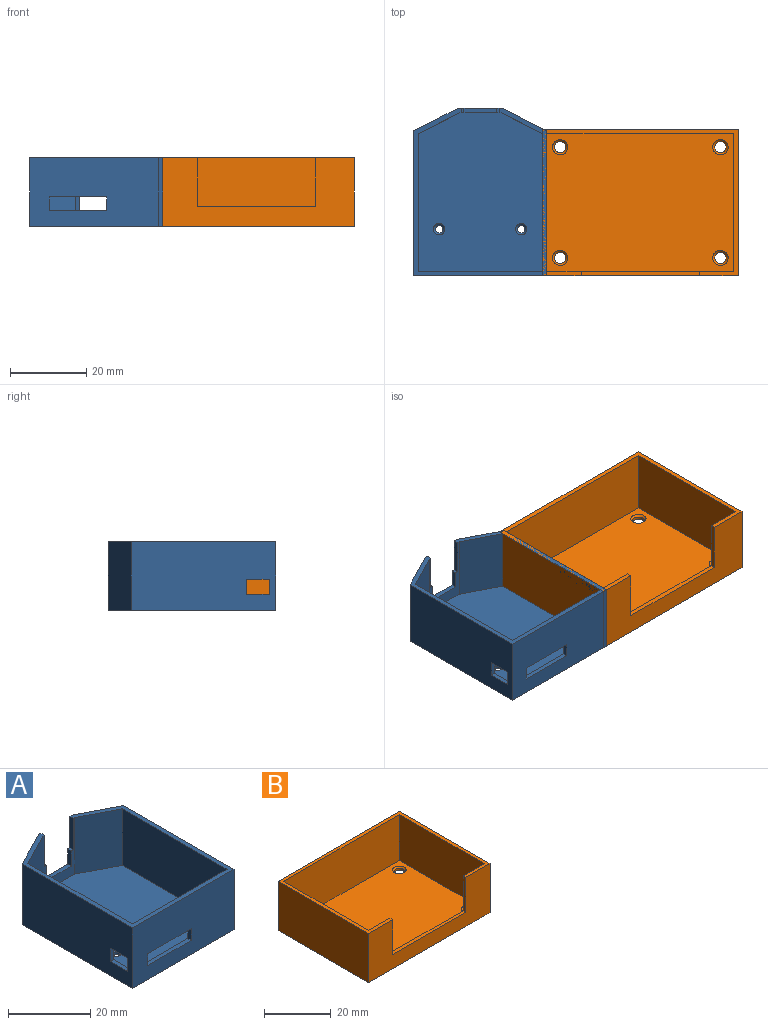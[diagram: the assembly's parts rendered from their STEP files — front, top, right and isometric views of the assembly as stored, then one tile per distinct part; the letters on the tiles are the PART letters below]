
ASSEMBLY  parts=2 mates=1
PART A: 34 faces, bbox 34.9x43.9x18 mm
  f0: plane 37.93x18mm, normal (-1,0,0), area 658.8mm2, adj f2,f4,f5,f9,f26,f27,f28,f29
  f1: plane 36x16.8mm, normal (1,0,0), area 580.8mm2, adj f3,f4,f10,f14,f26,f27,f28,f29
  f2: plane 34.9x18mm, normal (0,-1,0), area 575.7mm2, adj f0,f4,f6,f9,f22,f23,f24,f25
  f3: plane 32.5x16.8mm, normal (0,1,0), area 493.5mm2, adj f1,f4,f11,f14,f22,f23,f24,f25
  f4: plane 43.9x34.9mm, normal (0,0,1), area 160.9mm2, adj f0,f1,f2,f3,f5,f6,f7,f8
  f5: plane 18x11.66mm, normal (-0.46,0.89,0), area 235.8mm2, adj f0,f4,f8,f9
  f6: plane 37.93x18mm, normal (1,0,0), area 682.8mm2, adj f2,f4,f7,f9
  f7: plane 18x11.66mm, normal (0.46,0.89,0), area 235.8mm2, adj f4,f6,f8,f9
  f8: plane 18x11.58mm, normal (0,1,0), area 77.2mm2, adj f4,f5,f7,f9,f15,f16,f17,f18
  f9: plane 43.9x34.9mm, normal (0,0,-1), area 1456.3mm2, adj f0,f2,f5,f6,f7,f8,f30,f31
  f10: plane 16.8x10.75mm, normal (0.46,-0.89,0), area 202.9mm2, adj f1,f4,f13,f14
  f11: plane 36x16.8mm, normal (-1,0,0), area 604.8mm2, adj f3,f4,f12,f14
  f12: plane 16.8x10.75mm, normal (-0.46,-0.89,0), area 202.9mm2, adj f4,f11,f13,f14
  f13: plane 16.8x11mm, normal (0,-1,0), area 53.5mm2, adj f4,f10,f12,f14,f15,f16,f17,f18
  f14: plane 41.5x32.5mm, normal (0,0,1), area 1275.5mm2, adj f1,f3,f10,f11,f12,f13,f32,f33
  f15: plane 4.5x1.2mm, normal (1,0,0), area 5.4mm2, adj f8,f13,f16,f21
  f16: plane 1.2x0.75mm, normal (0,0,1), area 0.9mm2, adj f8,f13,f15,f17
  f17: plane 9.3x1.2mm, normal (1,0,0), area 11.2mm2, adj f4,f8,f13,f16
  f18: plane 9.3x1.2mm, normal (-1,0,0), area 11.2mm2, adj f4,f8,f13,f19
  f19: plane 1.2x0.75mm, normal (0,0,1), area 0.9mm2, adj f8,f13,f18,f20
  f20: plane 4.5x1.2mm, normal (-1,0,0), area 5.4mm2, adj f8,f13,f19,f21
  f21: plane 8.5x1.2mm, normal (0,0,1), area 10.2mm2, adj f8,f13,f15,f20
  f22: plane 15x1.2mm, normal (0,0,1), area 18mm2, adj f2,f3,f23,f25
  f23: plane 3.5x1.2mm, normal (-1,0,0), area 4.2mm2, adj f2,f3,f22,f24
  f24: plane 15x1.2mm, normal (0,0,-1), area 18mm2, adj f2,f3,f23,f25
  f25: plane 3.5x1.2mm, normal (1,0,0), area 4.2mm2, adj f2,f3,f22,f24
  f26: plane 4x1.2mm, normal (0,1,0), area 4.8mm2, adj f0,f1,f27,f29
  f27: plane 6x1.2mm, normal (0,0,-1), area 7.2mm2, adj f0,f1,f26,f28
  f28: plane 4x1.2mm, normal (0,-1,0), area 4.8mm2, adj f0,f1,f27,f29
  f29: plane 6x1.2mm, normal (0,0,1), area 7.2mm2, adj f0,f1,f26,f28
  f30: cylinder r=1mm len=2mm, axis (0,0,-1), area 4.4mm2, adj f9,f32
  f31: cylinder r=1mm len=2mm, axis (0,0,-1), area 4.4mm2, adj f9,f33
  f32: cone r=1.5mm half-angle=45deg, axis (0,0,1), area 5.6mm2, adj f14,f30
  f33: cone r=1.5mm half-angle=45deg, axis (0,0,1), area 5.6mm2, adj f14,f31
PART B: 22 faces, bbox 51.4x38.4x18 mm
  f0: plane 51.4x38.4mm, normal (0,0,1), area 172.6mm2, adj f1,f2,f3,f4,f5,f7,f8,f9
  f1: plane 51.4x18mm, normal (0,-1,0), area 528.4mm2, adj f0,f3,f4,f6,f15,f16,f17
  f2: plane 49x16.8mm, normal (0,1,0), area 426.4mm2, adj f0,f7,f8,f10,f15,f16,f17
  f3: plane 38.4x18mm, normal (-1,0,0), area 691.2mm2, adj f0,f1,f5,f6
  f4: plane 38.4x18mm, normal (1,0,0), area 691.2mm2, adj f0,f1,f5,f6
  f5: plane 51.4x18mm, normal (0,1,0), area 925.2mm2, adj f0,f3,f4,f6
  f6: plane 51.4x38.4mm, normal (0,0,-1), area 1945.5mm2, adj f1,f3,f4,f5,f11,f12,f13,f14
  f7: plane 36x16.8mm, normal (1,0,0), area 604.8mm2, adj f0,f2,f9,f10
  f8: plane 36x16.8mm, normal (-1,0,0), area 604.8mm2, adj f0,f2,f9,f10
  f9: plane 49x16.8mm, normal (0,-1,0), area 823.2mm2, adj f0,f7,f8,f10
  f10: plane 49x36mm, normal (0,0,1), area 1713.7mm2, adj f2,f7,f8,f9,f18,f19,f20,f21
  f11: cylinder r=1.5mm len=3mm, axis (0,0,-1), area 6.6mm2, adj f6,f20
  f12: cylinder r=1.5mm len=3mm, axis (0,0,-1), area 6.6mm2, adj f6,f19
  f13: cylinder r=1.5mm len=3mm, axis (0,0,-1), area 6.6mm2, adj f6,f21
  f14: cylinder r=1.5mm len=3mm, axis (0,0,-1), area 6.6mm2, adj f6,f18
  f15: plane 31x1.2mm, normal (0,0,1), area 37.2mm2, adj f1,f2,f16,f17
  f16: plane 12.8x1.2mm, normal (1,0,0), area 15.4mm2, adj f0,f1,f2,f15
  f17: plane 12.8x1.2mm, normal (-1,0,0), area 15.4mm2, adj f0,f1,f2,f15
  f18: cone r=2mm half-angle=45deg, axis (0,0,1), area 7.8mm2, adj f10,f14
  f19: cone r=2mm half-angle=45deg, axis (0,0,1), area 7.8mm2, adj f10,f12
  f20: cone r=2mm half-angle=45deg, axis (0,0,1), area 7.8mm2, adj f10,f11
  f21: cone r=2mm half-angle=45deg, axis (0,0,1), area 7.8mm2, adj f10,f13
PLACE A t=(-41.95,-18,0)mm
PLACE B at identity fixed
MATE fastened A.f11 <-> B.f3  axis (-1,0,0) through (-25.7,-18,9.6)mm
